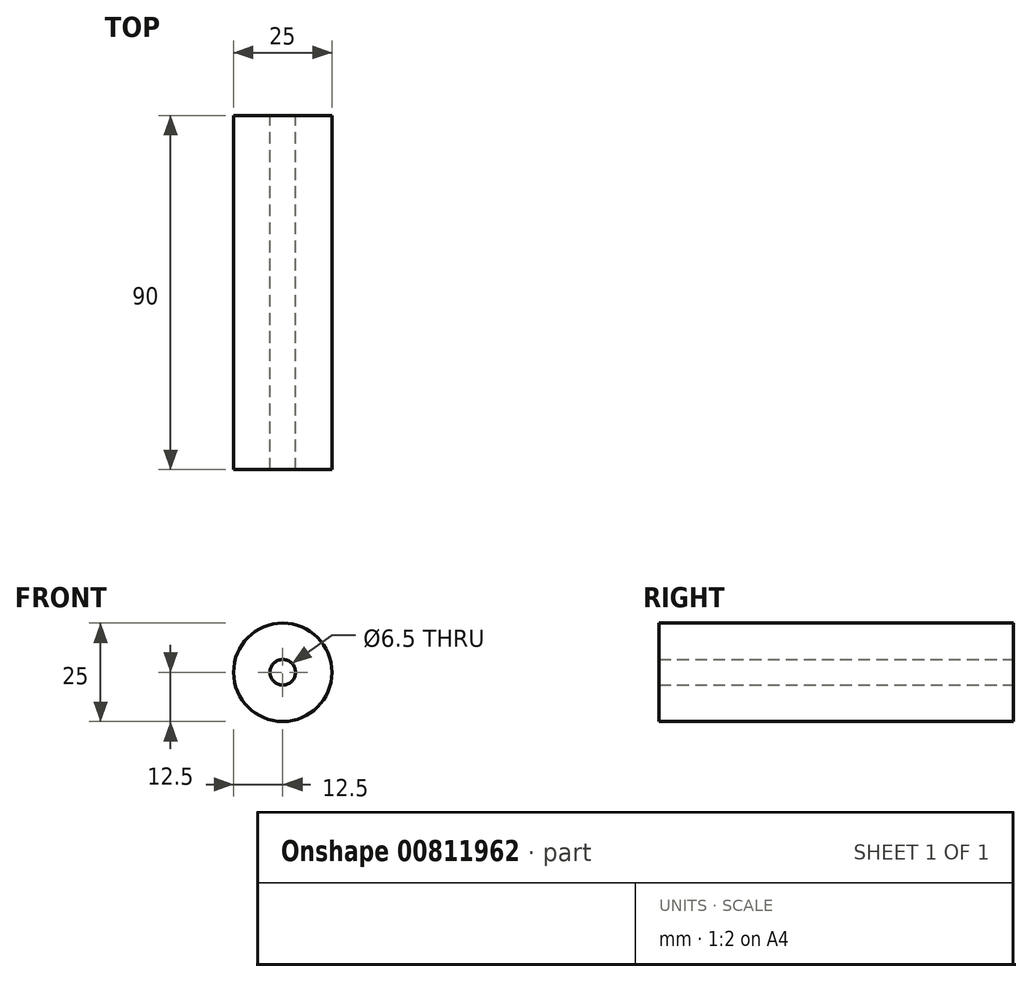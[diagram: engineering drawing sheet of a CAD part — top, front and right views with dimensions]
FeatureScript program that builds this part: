
annotation { "Feature Type Name" : "Feature", "Feature Type Description" : "" }
export const myFeature = defineFeature(function(context is Context, id is Id, definition is map)
    precondition{}
    {
        {
            var Q0;
            Q0=qCreatedBy(makeId("Front.planeOp"),FACE);
            var sketch = newSketch(context, id + "F0", { "sketchPlane" : qUnion([Q0])});
            skCircle(sketch, "E0", {"center": v(0, 0) * mm, "radius": 12.5 * mm});
            skCircle(sketch, "E1", {"center": v(0, 0) * mm, "radius": 3.25 * mm});
            skSolve(sketch);
        }
        {
            var Q0;
            Q0 = qSketchRegion(id + "F0", true);
            extrude(context, id + "F1", {"entities" : qUnion([Q0]), "depth" : 90 * mm, "offsetDistance" : 25 * mm});
        }
    });
